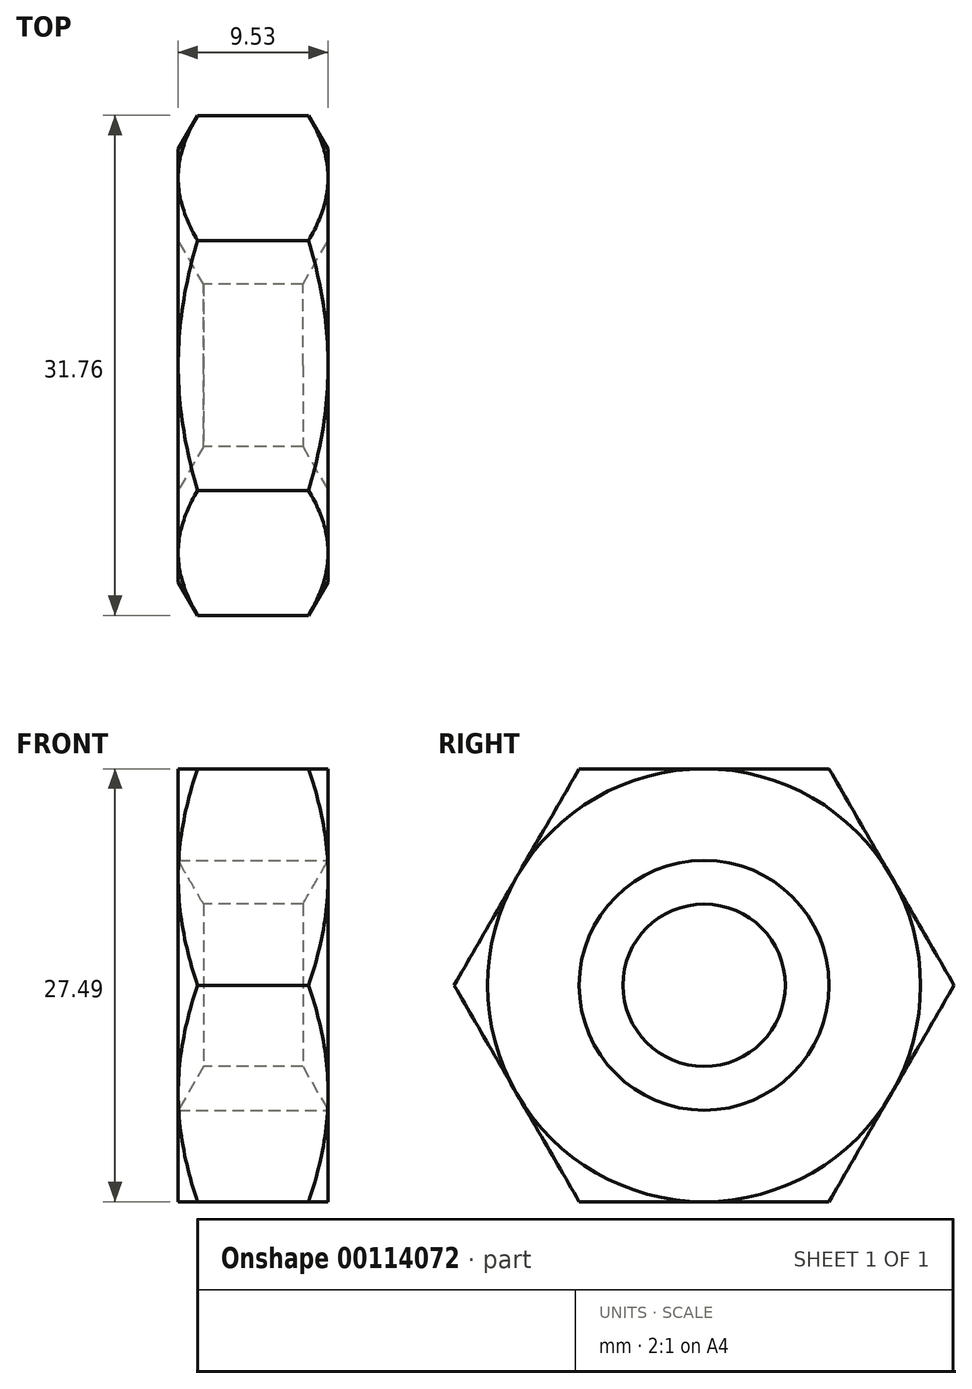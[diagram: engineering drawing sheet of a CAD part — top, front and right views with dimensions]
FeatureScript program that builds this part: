
annotation { "Feature Type Name" : "Feature", "Feature Type Description" : "" }
export const myFeature = defineFeature(function(context is Context, id is Id, definition is map)
    precondition{}
    {
        {
            var Q0;
            Q0=qCreatedBy(makeId("Front.planeOp"),FACE);
            var sketch = newSketch(context, id + "F0", { "sketchPlane" : qUnion([Q0])});
            skLineSegment(sketch, "E0", {"start": v(-85.6, 103.2) * mm, "end": v(149.2, 103.2) * mm, "construction": true});
            skLineSegment(sketch, "E1.top", {"start": v(78.06, 114.64) * mm, "end": v(5.04, 114.64) * mm});
            skLineSegment(sketch, "E2.top", {"start": v(78.06, 115.9) * mm, "end": v(86, 115.9) * mm});
            skLineSegment(sketch, "E2.left", {"start": v(78.06, 114.64) * mm, "end": v(78.06, 115.9) * mm});
            skLineSegment(sketch, "E2.right", {"start": v(86, 111.78) * mm, "end": v(86, 115.9) * mm});
            skLineSegment(sketch, "E3.bottom", {"start": v(-44.24, 108.36) * mm, "end": v(95.53, 108.36) * mm});
            skLineSegment(sketch, "E3.top", {"start": v(-44.24, 110.34) * mm, "end": v(-7.66, 110.34) * mm});
            skLineSegment(sketch, "E3.left", {"start": v(-44.24, 108.36) * mm, "end": v(-44.24, 110.34) * mm});
            skLineSegment(sketch, "E4.top", {"start": v(-7.66, 111.14) * mm, "end": v(5.04, 111.14) * mm});
            skLineSegment(sketch, "E4.left", {"start": v(-7.66, 110.34) * mm, "end": v(-7.66, 111.14) * mm});
            skLineSegment(sketch, "E5.trimOffspring", {"start": v(5.04, 111.14) * mm, "end": v(5.04, 114.64) * mm});
            skLineSegment(sketch, "E6.top", {"start": v(86, 111.78) * mm, "end": v(89.18, 111.78) * mm});
            skLineSegment(sketch, "E7.top", {"start": v(89.18, 112.73) * mm, "end": v(95.53, 112.73) * mm});
            skLineSegment(sketch, "E7.left", {"start": v(89.18, 111.78) * mm, "end": v(89.18, 112.73) * mm});
            skLineSegment(sketch, "E7.right", {"start": v(95.53, 108.36) * mm, "end": v(95.53, 112.73) * mm});
            skLineSegment(sketch, "E8", {"start": v(1.86, 111.14) * mm, "end": v(1.86, 130.9) * mm, "construction": true});
            skSolve(sketch);
        }
        {
            var Q0;
            Q0=qSketchRegion(id+"F0",true);
            var Q1;
            Q1=sQuery(id+"F0.wireOp",EDGE,"E0");
            revolve(context, id + "F1", {"entities" : qUnion([Q0]), "axis" : qUnion([Q1]), "revolveType" : RevolveType.FULL});
        }
        {
            var Q0;
            Q0=makeQuery(id+"F1.opRevolve","SWEPT_EDGE",EDGE,{"disambiguationData":[OSD([sQuery(id+"F0.wireOp",EDGE,"E7.top"),sQuery(id+"F0.wireOp",EDGE,"E7.right")])]});
            chamfer(context, id + "F2", {"entities" : qUnion([Q0]), "width" : 1.59 * mm, "tangentPropagation" : true});
        }
        {
            var Q0;
            Q0=makeQuery(id+"F1.opRevolve","SWEPT_FACE",FACE,{"disambiguationData":[OSD([sQuery(id+"F0.wireOp",EDGE,"E2.right")])]});
            var sketch = newSketch(context, id + "F3", { "sketchPlane" : qUnion([Q0])});
            skLineSegment(sketch, "E9", {"start": v(0, 103.2) * mm, "end": v(0, 115.9) * mm, "construction": true});
            skSolve(sketch);
        }
        {
            var Q0;
            Q0=qCreatedBy(makeId("Top.planeOp"),FACE);
            var Q1;
            Q1=sQuery(id+"F3.wireOp",VERTEX,"E9.end");
            cPlane(context, id + "F4", {"entities" : qUnion([Q0, Q1]), "cplaneType" : CPlaneType.PLANE_POINT, "offset" : 152.4 * mm, "width" : 152.4 * mm, "height" : 152.4 * mm});
        }
        {
            var Q0;
            Q0=qCreatedBy(id+"F4.planeOp",FACE);
            var sketch = newSketch(context, id + "F5", { "sketchPlane" : qUnion([Q0])});
            skLineSegment(sketch, "E10", {"start": v(78.06, 0) * mm, "end": v(86, 0) * mm, "construction": true});
            skPoint(sketch, "E11", {"position": v(82.03, 0) * mm});
            skSolve(sketch);
        }
        {
            var Q0;
            Q0=sQuery(id+"F5.wireOp",VERTEX,"E11");
            var Q1;
            Q1=makeQuery(id+"F1.opRevolve","SWEPT_BODY",BODY,{"disambiguationData":[OSD([sQuery(id+"F0.wireOp",EDGE,"E1.top"),sQuery(id+"F0.wireOp",EDGE,"E2.top"),sQuery(id+"F0.wireOp",EDGE,"E2.left"),sQuery(id+"F0.wireOp",EDGE,"E2.right"),sQuery(id+"F0.wireOp",EDGE,"E3.bottom"),sQuery(id+"F0.wireOp",EDGE,"E3.top"),sQuery(id+"F0.wireOp",EDGE,"E3.left"),sQuery(id+"F0.wireOp",EDGE,"E4.top"),sQuery(id+"F0.wireOp",EDGE,"E4.left"),sQuery(id+"F0.wireOp",EDGE,"E5.trimOffspring"),sQuery(id+"F0.wireOp",EDGE,"E6.top"),sQuery(id+"F0.wireOp",EDGE,"E7.top"),sQuery(id+"F0.wireOp",EDGE,"E7.left"),sQuery(id+"F0.wireOp",EDGE,"E7.right")])]});
            hole(context, id + "F6", {"style" : HoleStyle.SIMPLE, "endStyle" : HoleEndStyle.THROUGH, "holeDiameter" : 4.06 * mm, "locations" : qUnion([Q0]), "scope" : qUnion([Q1]), "isTappedThrough" : true});
        }
        {
            var Q0;
            Q0=makeQuery(id+"F1.opRevolve","SWEPT_FACE",FACE,{"disambiguationData":[OSD([sQuery(id+"F0.wireOp",EDGE,"E5.trimOffspring")])]});
            var sketch = newSketch(context, id + "F7", { "sketchPlane" : qUnion([Q0])});
            skCircle(sketch, "E12.cCircle", {"center": v(0, 103.2) * mm, "radius": 13.75 * mm, "construction": true});
            skLineSegment(sketch, "E12.0", {"start": v(-7.94, 116.95) * mm, "end": v(7.94, 116.95) * mm});
            skLineSegment(sketch, "E12.1", {"start": v(7.94, 116.95) * mm, "end": v(15.88, 103.2) * mm});
            skLineSegment(sketch, "E12.2", {"start": v(15.87, 103.2) * mm, "end": v(7.94, 89.46) * mm});
            skLineSegment(sketch, "E12.3", {"start": v(7.94, 89.46) * mm, "end": v(-7.94, 89.46) * mm});
            skLineSegment(sketch, "E12.4", {"start": v(-7.94, 89.46) * mm, "end": v(-15.87, 103.2) * mm});
            skLineSegment(sketch, "E12.5", {"start": v(-15.87, 103.2) * mm, "end": v(-7.94, 116.95) * mm});
            skPoint(sketch, "E12.0.midPoint", {"position": v(0, 116.95) * mm});
            skCircle(sketch, "E13", {"center": v(0, 103.2) * mm, "radius": 7.94 * mm});
            skSolve(sketch);
        }
        {
            var Q0;
            Q0=qSketchRegion(id+"F7",true);
            extrude(context, id + "F8", {"entities" : qUnion([Q0]), "depth" : 9.52 * mm});
        }
        {
            var Q0;
            Q0=makeQuery(id+"F8.opExtrude","CAP_FACE",FACE,{"disambiguationData":[OSD([sQuery(id+"F7.wireOp",EDGE,"E12.0"),sQuery(id+"F7.wireOp",EDGE,"E12.1"),sQuery(id+"F7.wireOp",EDGE,"E12.2"),sQuery(id+"F7.wireOp",EDGE,"E12.3"),sQuery(id+"F7.wireOp",EDGE,"E12.4"),sQuery(id+"F7.wireOp",EDGE,"E12.5"),sQuery(id+"F7.wireOp",EDGE,"E13")])],"isStart":false});
            var sketch = newSketch(context, id + "F9", { "sketchPlane" : qUnion([Q0])});
            skCircle(sketch, "E14", {"center": v(0, 103.2) * mm, "radius": 13.75 * mm});
            skSolve(sketch);
        }
        {
            var Q0;
            Q0=makeQuery(id+"F9.imprint","IMPRINT",FACE,{"disambiguationData":[TD([[makeQuery(id+"F9.imprint","IMPRINT",EDGE,{"derivedFrom":makeQuery(id+"F8.opExtrude","CAP_EDGE",EDGE,{"disambiguationData":[OSD([sQuery(id+"F7.wireOp",EDGE,"E13")])],"isStart":false})}),-1.0]])]});
            var Q1;
            Q1=sQuery(id+"F9.wireOp",EDGE,"E14");
            extrude(context, id + "F10", {"entities" : qUnion([Q0]), "operationType" : NewBodyOperationType.INTERSECT, "surfaceEntities" : qUnion([Q1]), "endBound" : BoundingType.UP_TO_NEXT, "oppositeDirection" : true, "depth" : 25.4 * mm, "hasDraft" : true, "draftAngle" : 60 * degree});
        }
        {
            var Q0;
            Q0=makeQuery(id+"F8.opExtrude","CAP_FACE",FACE,{"disambiguationData":[OSD([sQuery(id+"F7.wireOp",EDGE,"E12.0"),sQuery(id+"F7.wireOp",EDGE,"E12.1"),sQuery(id+"F7.wireOp",EDGE,"E12.2"),sQuery(id+"F7.wireOp",EDGE,"E12.3"),sQuery(id+"F7.wireOp",EDGE,"E12.4"),sQuery(id+"F7.wireOp",EDGE,"E12.5"),sQuery(id+"F7.wireOp",EDGE,"E13")])],"isStart":true});
            var sketch = newSketch(context, id + "F11", { "sketchPlane" : qUnion([Q0])});
            skCircle(sketch, "E15", {"center": v(0, 103.2) * mm, "radius": 13.75 * mm});
            skSolve(sketch);
        }
        {
            var Q0;
            Q0=makeQuery(id+"F11.imprint","IMPRINT",FACE,{"disambiguationData":[TD([[makeQuery(id+"F11.imprint","IMPRINT",EDGE,{"derivedFrom":makeQuery(id+"F8.opExtrude","CAP_EDGE",EDGE,{"disambiguationData":[OSD([sQuery(id+"F7.wireOp",EDGE,"E13")])],"isStart":true})}),1.0]])]});
            extrude(context, id + "F12", {"entities" : qUnion([Q0]), "operationType" : NewBodyOperationType.INTERSECT, "endBound" : BoundingType.UP_TO_NEXT, "oppositeDirection" : true, "depth" : 25.4 * mm, "hasDraft" : true, "draftAngle" : 60 * degree});
        }
    });
